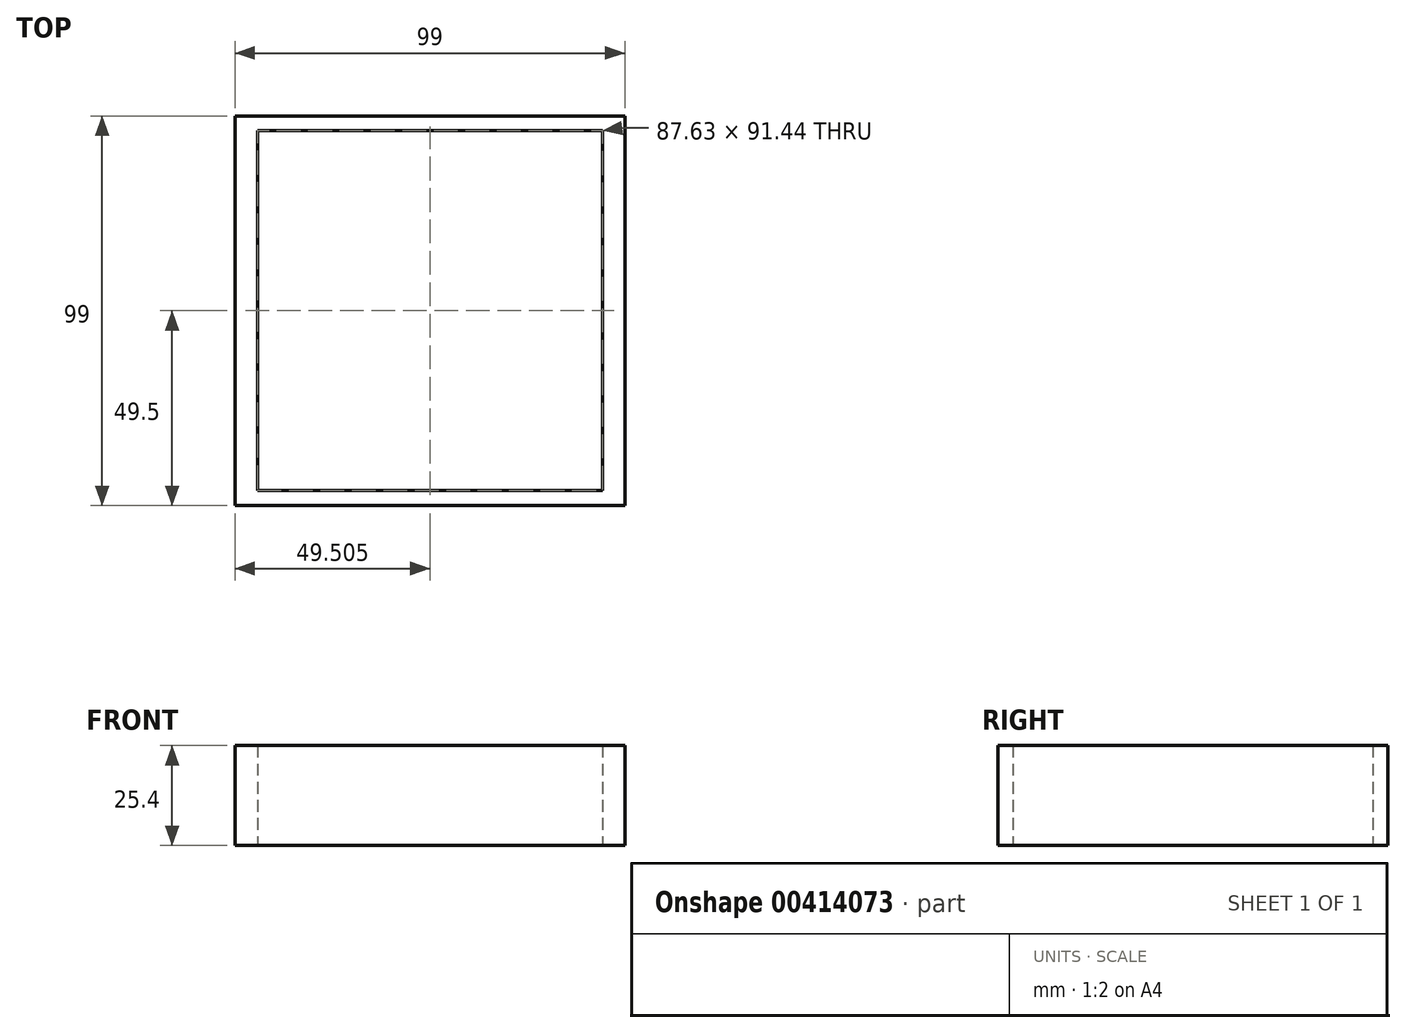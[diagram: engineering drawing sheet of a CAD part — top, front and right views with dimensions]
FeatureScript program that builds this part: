
annotation { "Feature Type Name" : "Feature", "Feature Type Description" : "" }
export const myFeature = defineFeature(function(context is Context, id is Id, definition is map)
    precondition{}
    {
        {
            var Q0;
            Q0=qCreatedBy(makeId("Top.planeOp"),FACE);
            var sketch = newSketch(context, id + "F0", { "sketchPlane" : qUnion([Q0])});
            skLineSegment(sketch, "E0.bottom", {"start": v(0, 0) * mm, "end": v(87.63, 0) * mm});
            skLineSegment(sketch, "E0.top", {"start": v(0, 91.44) * mm, "end": v(87.63, 91.44) * mm});
            skLineSegment(sketch, "E0.left", {"start": v(0, 0) * mm, "end": v(0, 91.44) * mm});
            skLineSegment(sketch, "E0.right", {"start": v(87.63, 0) * mm, "end": v(87.63, 91.44) * mm});
            skPoint(sketch, "E1", {"position": v(43.82, 45.72) * mm});
            skPoint(sketch, "E2.orphan", {"position": v(43.82, 91.44) * mm});
            skPoint(sketch, "E3.end.orphan", {"position": v(0, 45.72) * mm});
            skPoint(sketch, "E4.end.orphan", {"position": v(43.82, 0) * mm});
            skPoint(sketch, "E5.end.orphan", {"position": v(87.63, 45.72) * mm});
            skLineSegment(sketch, "E6.bottom", {"start": v(93.32, 95.22) * mm, "end": v(-5.68, 95.22) * mm});
            skLineSegment(sketch, "E6.top", {"start": v(93.32, -3.78) * mm, "end": v(-5.68, -3.78) * mm});
            skLineSegment(sketch, "E6.left", {"start": v(93.32, 95.22) * mm, "end": v(93.32, -3.78) * mm});
            skLineSegment(sketch, "E6.right", {"start": v(-5.68, 95.22) * mm, "end": v(-5.68, -3.78) * mm});
            skSolve(sketch);
        }
        {
            var Q0;
            Q0=makeQuery(id+"F0.imprint","IMPRINT",FACE,{"disambiguationData":[TD([[makeQuery(id+"F0.imprint","IMPRINT",EDGE,{"derivedFrom":sQuery(id+"F0.wireOp",EDGE,"E0.bottom")}),-1.0]])]});
            extrude(context, id + "F1", {"entities" : qUnion([Q0]), "depth" : 25.4 * mm});
        }
    });
